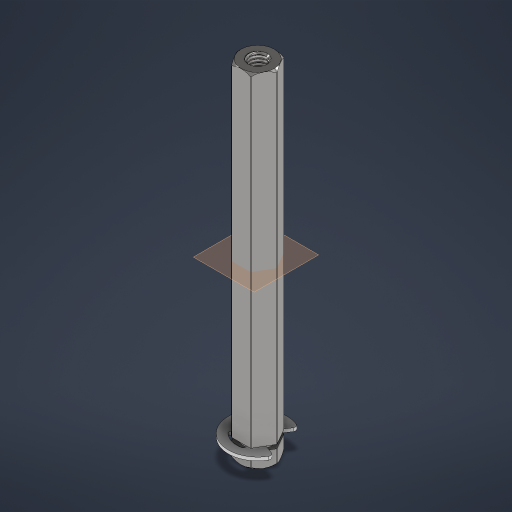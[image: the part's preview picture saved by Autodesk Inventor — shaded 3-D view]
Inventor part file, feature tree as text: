
AUTODESK INVENTOR PART (.ipt)
format: ipt  version: 2024 (Build 280153000, 153)  size: 976,896 bytes
history: native  units: in
note: dims shown in document units (in); Inventor stores cm internally (conversion verified against a paired STEP export)
features: plane x1, other x1
ambient origin geometry x8: Origin, YZ Plane, XZ Plane, XY Plane, X Axis, Y Axis, Z Axis, Center Point
bodies: Solid1 (feature_tree), Solid2 (feature_tree)
feature tree (2):
  plane  "Work Plane1"
  other  "2106 Series 8mm REX e-clip_2:1"
